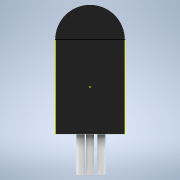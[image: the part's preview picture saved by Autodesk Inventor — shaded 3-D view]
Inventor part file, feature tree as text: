
AUTODESK INVENTOR PART (.ipt)
format: ipt  version: 2021 (Build 250183000, 183)  size: 124,928 bytes
history: native  units: mm
features: extrude x3, sketch x3
ambient origin geometry x8: Origin, YZ Plane, XZ Plane, XY Plane, X Axis, Y Axis, Z Axis, Center Point
bodies: Solid1 (feature_tree)
feature tree (6):
  extrude  "Extrusion1"  Depth=17.0mm
  sketch  "Sketch3"  dims[d2=8.0mm d3=0.0mm d4=2.0mm]
  sketch  "Sketch4"  dims[d6=2.0mm d7=10.0mm d8=0.0mm d9=2.0mm d10=10.0mm d11=0.0mm]
  extrude  "Extrusion2"  Depth=8.0mm
  extrude  "Extrusion3"  Depth=10.0mm TaperAngle=0.0deg
  sketch  "Sketch1"  dims[d0=23.0mm d1=17.0mm]
